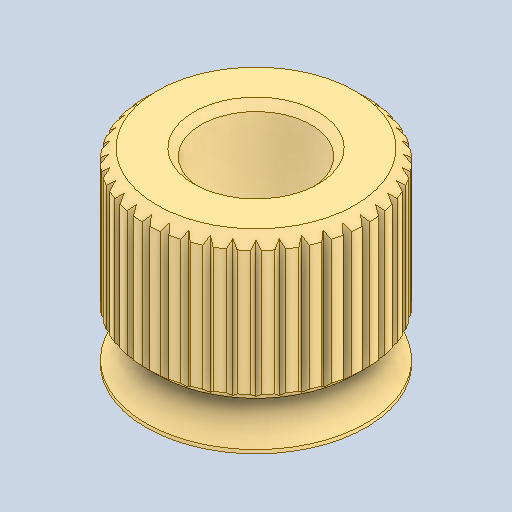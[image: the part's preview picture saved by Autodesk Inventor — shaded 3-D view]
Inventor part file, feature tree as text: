
AUTODESK INVENTOR PART (.ipt)
format: ipt  version: 2022 (Build 260153000, 153)  size: 324,608 bytes
history: mixed  units: mm
features: other x1, chamfer x1, imported_body x1
ambient origin geometry x8: Origin, YZ Plane, XZ Plane, XY Plane, X Axis, Y Axis, Z Axis, Center Point
bodies: Body1 (imported_parasolid)
feature tree (3):
  other  "Твердое тело1"
  chamfer  "Chaflán3"  [1 undecoded]
  imported_body  NMx_Import_Brep_tag  [imported B-rep: ~11 faces, bbox_mm=[0.225983, 3.4, 0.695506]]
note: 1 required parameter value undecoded (feature->parameter linkage not recoverable at this tier; creation-order binding heuristic only, values carry confidence <= 0.55)
